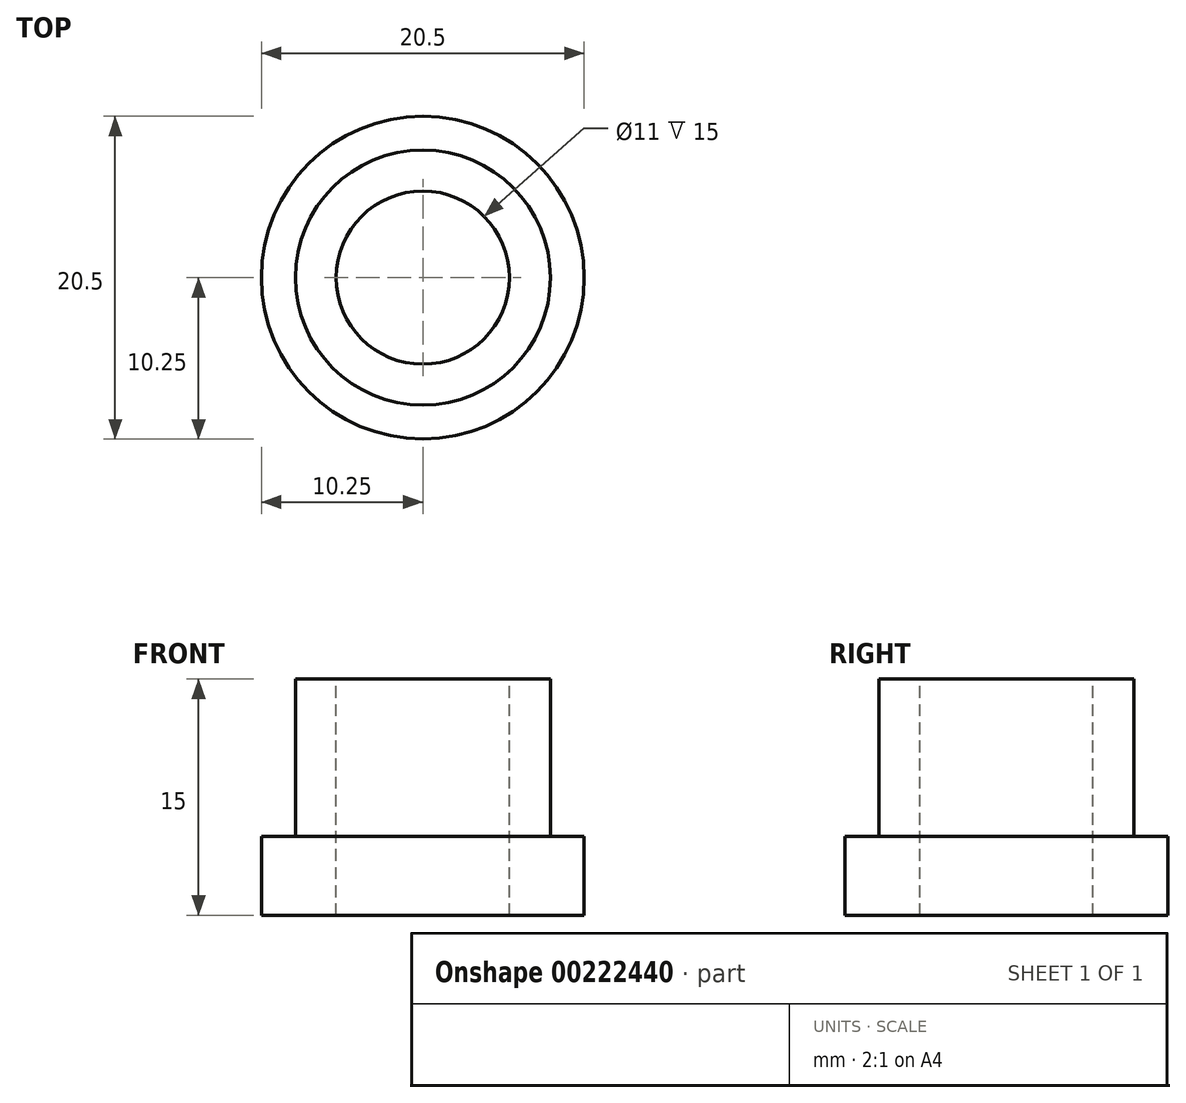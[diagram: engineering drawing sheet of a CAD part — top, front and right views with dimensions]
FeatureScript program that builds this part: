
annotation { "Feature Type Name" : "Feature", "Feature Type Description" : "" }
export const myFeature = defineFeature(function(context is Context, id is Id, definition is map)
    precondition{}
    {
        {
            var Q0;
            Q0=qCreatedBy(makeId("Front.planeOp"),FACE);
            var sketch = newSketch(context, id + "F0", { "sketchPlane" : qUnion([Q0])});
            skLineSegment(sketch, "E0", {"start": v(0, 78.33) * mm, "end": v(0, -82.12) * mm, "construction": true});
            skLineSegment(sketch, "E1", {"start": v(-5.5, 0) * mm, "end": v(-10.25, 0) * mm});
            skLineSegment(sketch, "E2", {"start": v(-10.25, 0) * mm, "end": v(-10.25, 5) * mm});
            skLineSegment(sketch, "E3", {"start": v(-10.25, 5) * mm, "end": v(-8.1, 5) * mm});
            skLineSegment(sketch, "E4", {"start": v(-8.1, 5) * mm, "end": v(-8.1, 15) * mm});
            skLineSegment(sketch, "E5", {"start": v(-8.1, 15) * mm, "end": v(-5.5, 15) * mm});
            skLineSegment(sketch, "E6", {"start": v(-5.5, 15) * mm, "end": v(-5.5, 0) * mm});
            skSolve(sketch);
        }
        {
            var Q0;
            Q0 = qSketchRegion(id + "F0", true);
            var Q1;
            Q1=sQuery(id+"F0.wireOp",EDGE,"E0");
            revolve(context, id + "F1", {"entities" : qUnion([Q0]), "axis" : qUnion([Q1]), "revolveType" : RevolveType.FULL});
        }
    });
